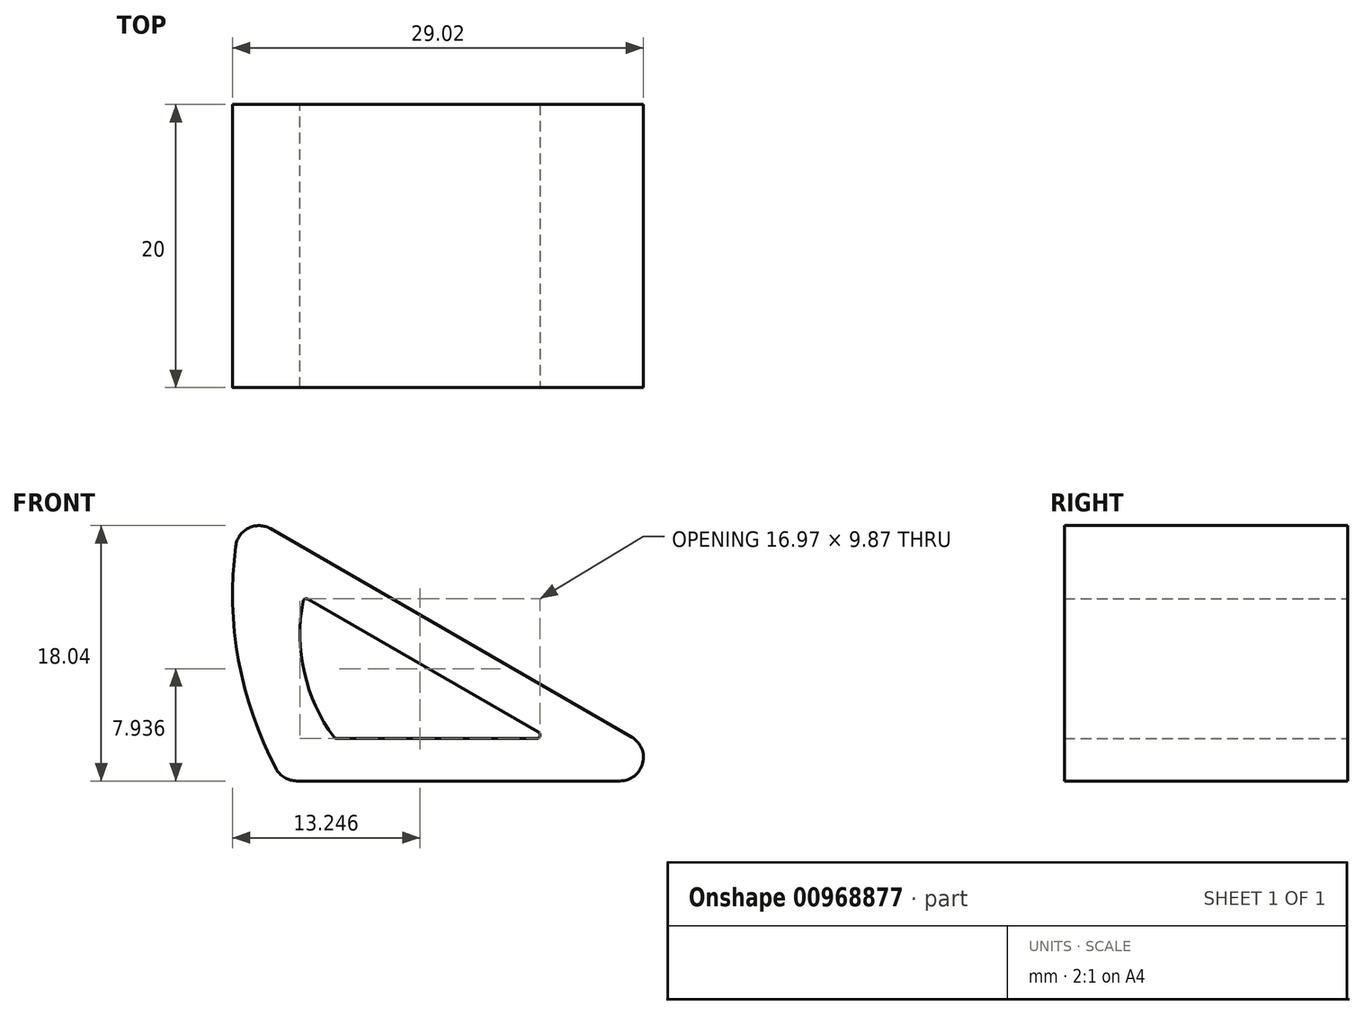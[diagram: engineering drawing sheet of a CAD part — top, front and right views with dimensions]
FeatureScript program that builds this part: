
annotation { "Feature Type Name" : "Feature", "Feature Type Description" : "" }
export const myFeature = defineFeature(function(context is Context, id is Id, definition is map)
    precondition{}
    {
        {
            var Q0;
            Q0=qCreatedBy(makeId("Front.planeOp"),FACE);
            var sketch = newSketch(context, id + "F0", { "sketchPlane" : qUnion([Q0])});
            skLineSegment(sketch, "E0", {"start": v(-41.6, -0.7) * mm, "end": v(-11.6, -0.7) * mm});
            skLineSegment(sketch, "E1", {"start": v(-44.5, 18.3) * mm, "end": v(-11.6, -0.7) * mm});
            skLineSegment(sketch, "E2", {"start": v(-40.12, 12.3) * mm, "end": v(-22.8, 2.3) * mm});
            skLineSegment(sketch, "E3", {"start": v(-22.8, 2.3) * mm, "end": v(-37.93, 2.3) * mm});
            skArc(sketch, "E4", {"start": v(-44.5, 18.3) * mm, "mid": v(-44.86, 8.52) * mm, "end": v(-41.6, -0.7) * mm});
            skArc(sketch, "E5", {"start": v(-40.12, 12.3) * mm, "mid": v(-40.11, 7.06) * mm, "end": v(-37.93, 2.3) * mm});
            skSolve(sketch);
        }
        {
            var Q0;
            Q0=makeQuery(id+"F0.imprint","IMPRINT",FACE,{"disambiguationData":[TD([[makeQuery(id+"F0.imprint","IMPRINT",EDGE,{"derivedFrom":sQuery(id+"F0.wireOp",EDGE,"E0")}),1.0]])]});
            extrude(context, id + "F1", {"entities" : qUnion([Q0]), "depth" : 20 * mm, "offsetDistance" : 25 * mm});
        }
        {
            var Q0;
            Q0=makeQuery(id+"F1.opExtrude","SWEPT_EDGE",EDGE,{"disambiguationData":[OSD([sQuery(id+"F0.wireOp",EDGE,"E1"),sQuery(id+"F0.wireOp",EDGE,"6fR0hKrW-n6GD-Bz1a-hcDN-633D6s9dCkdp")])]});
            var Q1;
            Q1=makeQuery(id+"F1.opExtrude","SWEPT_EDGE",EDGE,{"disambiguationData":[OSD([sQuery(id+"F0.wireOp",EDGE,"E0"),sQuery(id+"F0.wireOp",EDGE,"6fR0hKrW-n6GD-Bz1a-hcDN-633D6s9dCkdp")])]});
            var Q2;
            Q2=makeQuery(id+"F1.opExtrude","SWEPT_EDGE",EDGE,{"disambiguationData":[OSD([sQuery(id+"F0.wireOp",EDGE,"E0"),sQuery(id+"F0.wireOp",EDGE,"E1")])]});
            fillet(context, id + "F2", {"entities" : qUnion([Q0, Q1, Q2]), "radius" : 1.66 * mm, "tangentPropagation" : true, "allowEdgeOverflow" : false});
        }
        {
            var Q0;
            Q0=makeQuery(id+"F1.opExtrude","SWEPT_EDGE",EDGE,{"disambiguationData":[OSD([sQuery(id+"F0.wireOp",EDGE,"9OML1RmV-QH0V-nMhn-Kkrj-0wJA4CVymfOU"),sQuery(id+"F0.wireOp",EDGE,"E3")])]});
            var Q1;
            Q1=makeQuery(id+"F1.opExtrude","SWEPT_EDGE",EDGE,{"disambiguationData":[OSD([sQuery(id+"F0.wireOp",EDGE,"9OML1RmV-QH0V-nMhn-Kkrj-0wJA4CVymfOU"),sQuery(id+"F0.wireOp",EDGE,"E2")])]});
            var Q2;
            Q2=makeQuery(id+"F1.opExtrude","SWEPT_EDGE",EDGE,{"disambiguationData":[OSD([sQuery(id+"F0.wireOp",EDGE,"E2"),sQuery(id+"F0.wireOp",EDGE,"E3")])]});
            fillet(context, id + "F3", {"entities" : qUnion([Q0, Q1, Q2]), "radius" : 0.23 * mm, "tangentPropagation" : true, "allowEdgeOverflow" : false});
        }
    });
